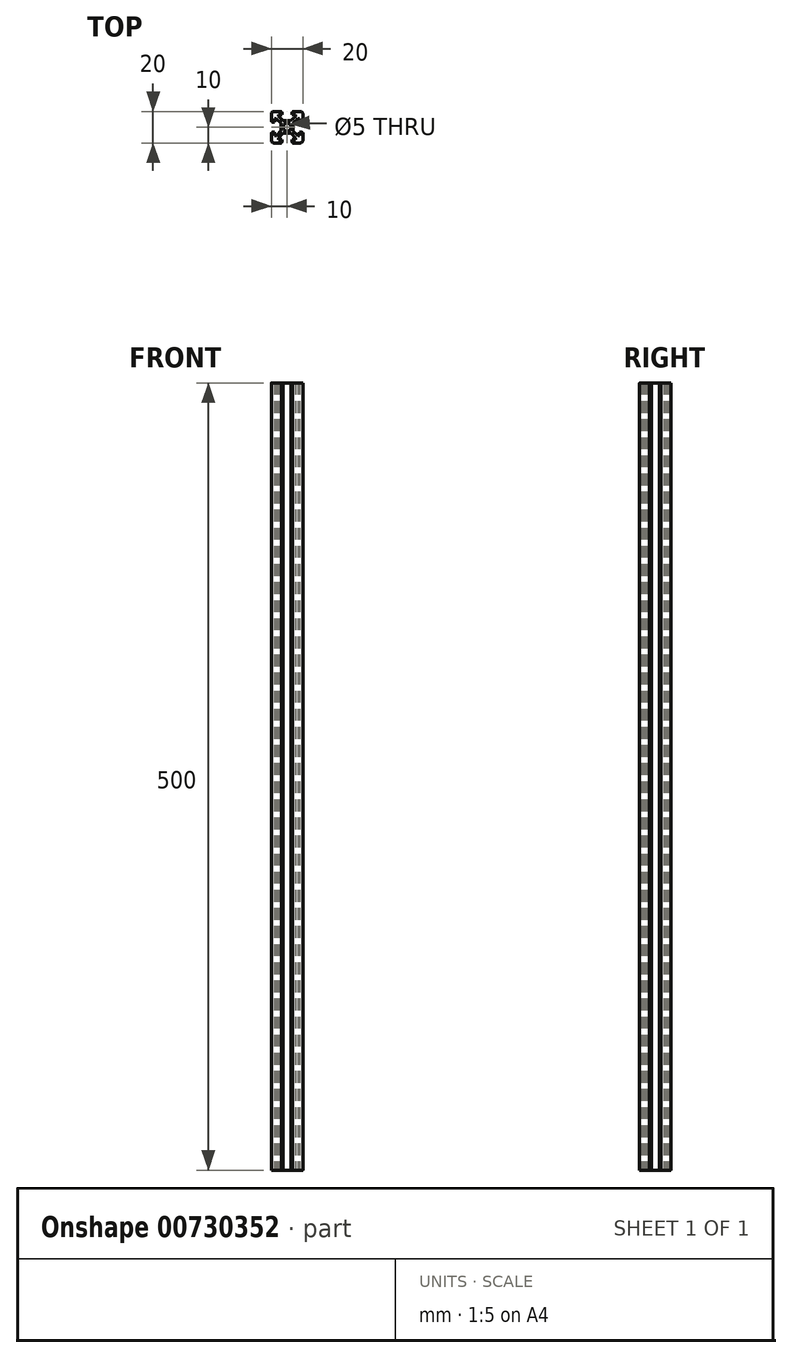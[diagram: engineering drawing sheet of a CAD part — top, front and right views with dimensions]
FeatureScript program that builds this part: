
annotation { "Feature Type Name" : "Feature", "Feature Type Description" : "" }
export const myFeature = defineFeature(function(context is Context, id is Id, definition is map)
    precondition{}
    {
        {
            var Q0;
            Q0=qCreatedBy(makeId("Top.planeOp"),FACE);
            var sketch = newSketch(context, id + "F0", { "sketchPlane" : qUnion([Q0])});
            skLineSegment(sketch, "E0.bottom", {"start": v(-8.5, 10) * mm, "end": v(-3.6, 10) * mm});
            skLineSegment(sketch, "E0.top", {"start": v(-8.5, -10) * mm, "end": v(-3.6, -10) * mm});
            skLineSegment(sketch, "E0.left", {"start": v(-10, 8.5) * mm, "end": v(-10, 3.6) * mm});
            skLineSegment(sketch, "E0.right", {"start": v(10, 8.5) * mm, "end": v(10, 3.6) * mm});
            skArc(sketch, "E1.filletArc", {"start": v(-8.5, 10) * mm, "mid": v(-9.56, 9.56) * mm, "end": v(-10, 8.5) * mm});
            skArc(sketch, "E2.filletArc", {"start": v(10, 8.5) * mm, "mid": v(9.56, 9.56) * mm, "end": v(8.5, 10) * mm});
            skArc(sketch, "E3.filletArc", {"start": v(8.5, -10) * mm, "mid": v(9.56, -9.56) * mm, "end": v(10, -8.5) * mm});
            skArc(sketch, "E4.filletArc", {"start": v(-10, -8.5) * mm, "mid": v(-9.56, -9.56) * mm, "end": v(-8.5, -10) * mm});
            skLineSegment(sketch, "E5.bottom", {"start": v(-5.5, 8) * mm, "end": v(-3.1, 8) * mm});
            skLineSegment(sketch, "E5.top", {"start": v(-5.5, -8) * mm, "end": v(-3.1, -8) * mm});
            skLineSegment(sketch, "E5.left", {"start": v(-8, 5.5) * mm, "end": v(-8, 3.1) * mm});
            skLineSegment(sketch, "E5.right", {"start": v(8, 5.5) * mm, "end": v(8, 3.1) * mm});
            skCircle(sketch, "E6", {"center": v(0, 0) * mm, "radius": 2.5 * mm});
            skLineSegment(sketch, "E7.right", {"start": v(5.5, -8) * mm, "end": v(5.5, -6.91) * mm});
            skLineSegment(sketch, "E8.top", {"start": v(8, 5.5) * mm, "end": v(7.01, 5.5) * mm});
            skLineSegment(sketch, "E9.bottom", {"start": v(-2.59, 4) * mm, "end": v(2.29, 4) * mm});
            skLineSegment(sketch, "E9.top", {"start": v(-2.67, -3.8) * mm, "end": v(2.39, -3.8) * mm});
            skLineSegment(sketch, "E9.left", {"start": v(-4, 2.59) * mm, "end": v(-4, -2.29) * mm});
            skLineSegment(sketch, "E9.right", {"start": v(3.8, 2.67) * mm, "end": v(3.8, -2.39) * mm});
            skLineSegment(sketch, "E10.trimOffspring", {"start": v(8, -5.5) * mm, "end": v(6.91, -5.5) * mm});
            skLineSegment(sketch, "E11.trimOffspring", {"start": v(-5.5, -8) * mm, "end": v(-5.5, -7.01) * mm});
            skLineSegment(sketch, "E12.left", {"start": v(-3.1, 9.5) * mm, "end": v(-3.1, 8) * mm});
            skLineSegment(sketch, "E12.right", {"start": v(3.1, 9.5) * mm, "end": v(3.1, 8) * mm});
            skLineSegment(sketch, "E13.trimOffspring", {"start": v(3.6, 10) * mm, "end": v(8.5, 10) * mm});
            skLineSegment(sketch, "E14.trimOffspring", {"start": v(3.1, 8) * mm, "end": v(5.5, 8) * mm});
            skLineSegment(sketch, "E15.left", {"start": v(-3.1, -9.5) * mm, "end": v(-3.1, -8) * mm});
            skLineSegment(sketch, "E15.right", {"start": v(3.1, -9.5) * mm, "end": v(3.1, -8) * mm});
            skLineSegment(sketch, "E16.trimOffspring", {"start": v(3.1, -8) * mm, "end": v(5.5, -8) * mm});
            skLineSegment(sketch, "E17.trimOffspring", {"start": v(3.6, -10) * mm, "end": v(8.5, -10) * mm});
            skLineSegment(sketch, "E18.bottom", {"start": v(9.5, 3.1) * mm, "end": v(8, 3.1) * mm});
            skLineSegment(sketch, "E18.top", {"start": v(9.5, -3.1) * mm, "end": v(8, -3.1) * mm});
            skLineSegment(sketch, "E19.trimOffspring", {"start": v(8, -3.1) * mm, "end": v(8, -5.5) * mm});
            skLineSegment(sketch, "E20.trimOffspring", {"start": v(10, -3.6) * mm, "end": v(10, -8.5) * mm});
            skLineSegment(sketch, "E21.bottom", {"start": v(-9.5, 3.1) * mm, "end": v(-8, 3.1) * mm});
            skLineSegment(sketch, "E21.top", {"start": v(-9.5, -3.1) * mm, "end": v(-8, -3.1) * mm});
            skLineSegment(sketch, "E22.trimOffspring", {"start": v(-10, -3.6) * mm, "end": v(-10, -8.5) * mm});
            skLineSegment(sketch, "E23.trimOffspring", {"start": v(-8, -3.1) * mm, "end": v(-8, -5.5) * mm});
            skLineSegment(sketch, "E24.top", {"start": v(-3.6, -9.5) * mm, "end": v(-3.1, -9.5) * mm});
            skLineSegment(sketch, "E24.left", {"start": v(-3.6, -10) * mm, "end": v(-3.6, -9.5) * mm});
            skLineSegment(sketch, "E24.right", {"start": v(3.6, -10) * mm, "end": v(3.6, -9.5) * mm});
            skLineSegment(sketch, "E25.trimOffspring", {"start": v(3.1, -9.5) * mm, "end": v(3.6, -9.5) * mm});
            skLineSegment(sketch, "E26.trimOffspring", {"start": v(-6.91, 5.5) * mm, "end": v(-8, 5.5) * mm});
            skLineSegment(sketch, "E27.trimOffspring", {"start": v(-5.5, 6.91) * mm, "end": v(-5.5, 8) * mm});
            skLineSegment(sketch, "E28.trimOffspring", {"start": v(-6.83, -5.5) * mm, "end": v(-8, -5.5) * mm});
            skLineSegment(sketch, "E29.trimOffspring", {"start": v(5.5, 6.83) * mm, "end": v(5.5, 8) * mm});
            skLineSegment(sketch, "E30.bottom", {"start": v(-10, 3.6) * mm, "end": v(-9.5, 3.6) * mm});
            skLineSegment(sketch, "E30.top", {"start": v(-10, -3.6) * mm, "end": v(-9.5, -3.6) * mm});
            skLineSegment(sketch, "E30.right", {"start": v(-9.5, 3.6) * mm, "end": v(-9.5, 3.1) * mm});
            skLineSegment(sketch, "E31.trimOffspring", {"start": v(-9.5, -3.1) * mm, "end": v(-9.5, -3.6) * mm});
            skLineSegment(sketch, "E32.top", {"start": v(-3.6, 9.5) * mm, "end": v(-3.1, 9.5) * mm});
            skLineSegment(sketch, "E32.left", {"start": v(-3.6, 10) * mm, "end": v(-3.6, 9.5) * mm});
            skLineSegment(sketch, "E32.right", {"start": v(3.6, 10) * mm, "end": v(3.6, 9.5) * mm});
            skLineSegment(sketch, "E33.trimOffspring", {"start": v(3.1, 9.5) * mm, "end": v(3.6, 9.5) * mm});
            skLineSegment(sketch, "E34", {"start": v(9.5, 3.1) * mm, "end": v(9.5, 3.6) * mm});
            skLineSegment(sketch, "E35", {"start": v(9.5, 3.6) * mm, "end": v(10, 3.6) * mm});
            skLineSegment(sketch, "E36", {"start": v(9.5, -3.1) * mm, "end": v(9.5, -3.6) * mm});
            skLineSegment(sketch, "E37", {"start": v(9.5, -3.6) * mm, "end": v(10, -3.6) * mm});
            skLineSegment(sketch, "E38.0", {"start": v(5.5, 6.83) * mm, "end": v(2.29, 4) * mm});
            skLineSegment(sketch, "E39.0", {"start": v(7.01, 5.5) * mm, "end": v(3.8, 2.67) * mm});
            skLineSegment(sketch, "E40.0", {"start": v(-6.91, 5.5) * mm, "end": v(-4, 2.59) * mm});
            skLineSegment(sketch, "E41.0", {"start": v(-5.5, 6.91) * mm, "end": v(-2.59, 4) * mm});
            skLineSegment(sketch, "E42.0", {"start": v(-5.5, -7.01) * mm, "end": v(-2.67, -3.8) * mm});
            skLineSegment(sketch, "E43.0", {"start": v(-6.83, -5.5) * mm, "end": v(-4, -2.29) * mm});
            skLineSegment(sketch, "E44.0", {"start": v(6.91, -5.5) * mm, "end": v(3.8, -2.39) * mm});
            skLineSegment(sketch, "E45.0", {"start": v(5.5, -6.91) * mm, "end": v(2.39, -3.8) * mm});
            skSolve(sketch);
        }
        {
            var Q0;
            Q0 = qSketchRegion(id + "F0", true);
            extrude(context, id + "F1", {"entities" : qUnion([Q0]), "depth" : 500 * mm, "offsetDistance" : 25 * mm});
        }
    });
